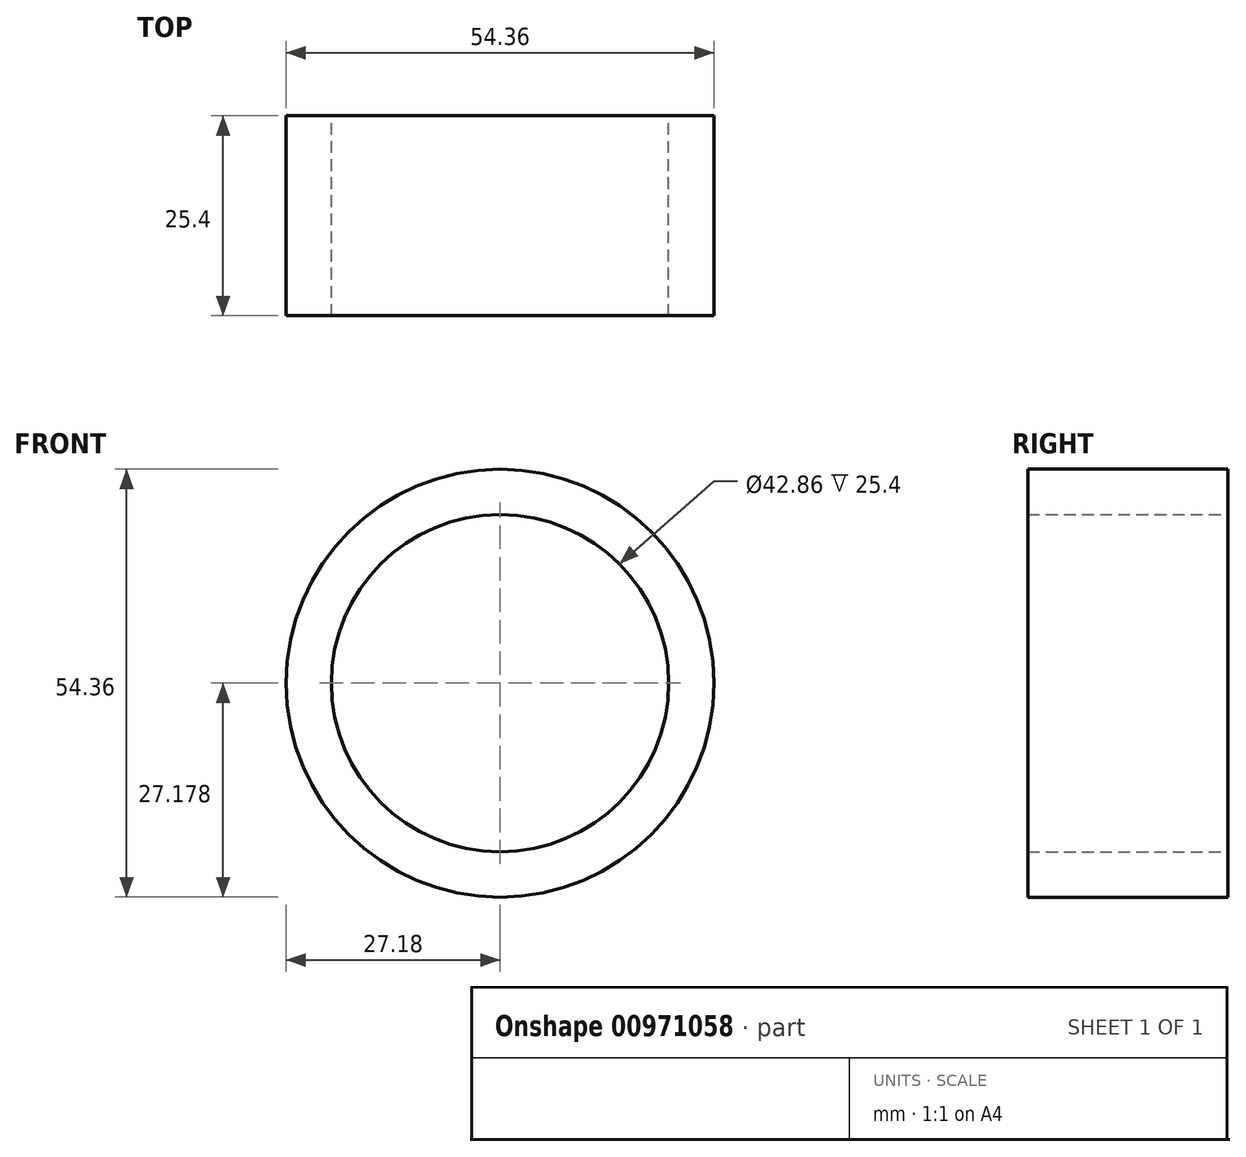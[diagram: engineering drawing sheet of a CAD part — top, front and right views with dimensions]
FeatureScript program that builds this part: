
annotation { "Feature Type Name" : "Feature", "Feature Type Description" : "" }
export const myFeature = defineFeature(function(context is Context, id is Id, definition is map)
    precondition{}
    {
        {
            var Q0;
            Q0=qCreatedBy(makeId("Front.planeOp"),FACE);
            var sketch = newSketch(context, id + "F0", { "sketchPlane" : qUnion([Q0])});
            skCircle(sketch, "E0", {"center": v(35.38, -42.41) * mm, "radius": 21.43 * mm});
            skCircle(sketch, "E1", {"center": v(35.38, -42.41) * mm, "radius": 27.18 * mm});
            skSolve(sketch);
        }
        {
            var Q0;
            Q0=makeQuery(id+"F0.imprint","IMPRINT",FACE,{"disambiguationData":[TD([[makeQuery(id+"F0.imprint","IMPRINT",EDGE,{"derivedFrom":sQuery(id+"F0.wireOp",EDGE,"E0")}),-1.0]])]});
            extrude(context, id + "F1", {"entities" : qUnion([Q0]), "depth" : 25.4 * mm, "offsetDistance" : 25.4 * mm});
        }
    });
